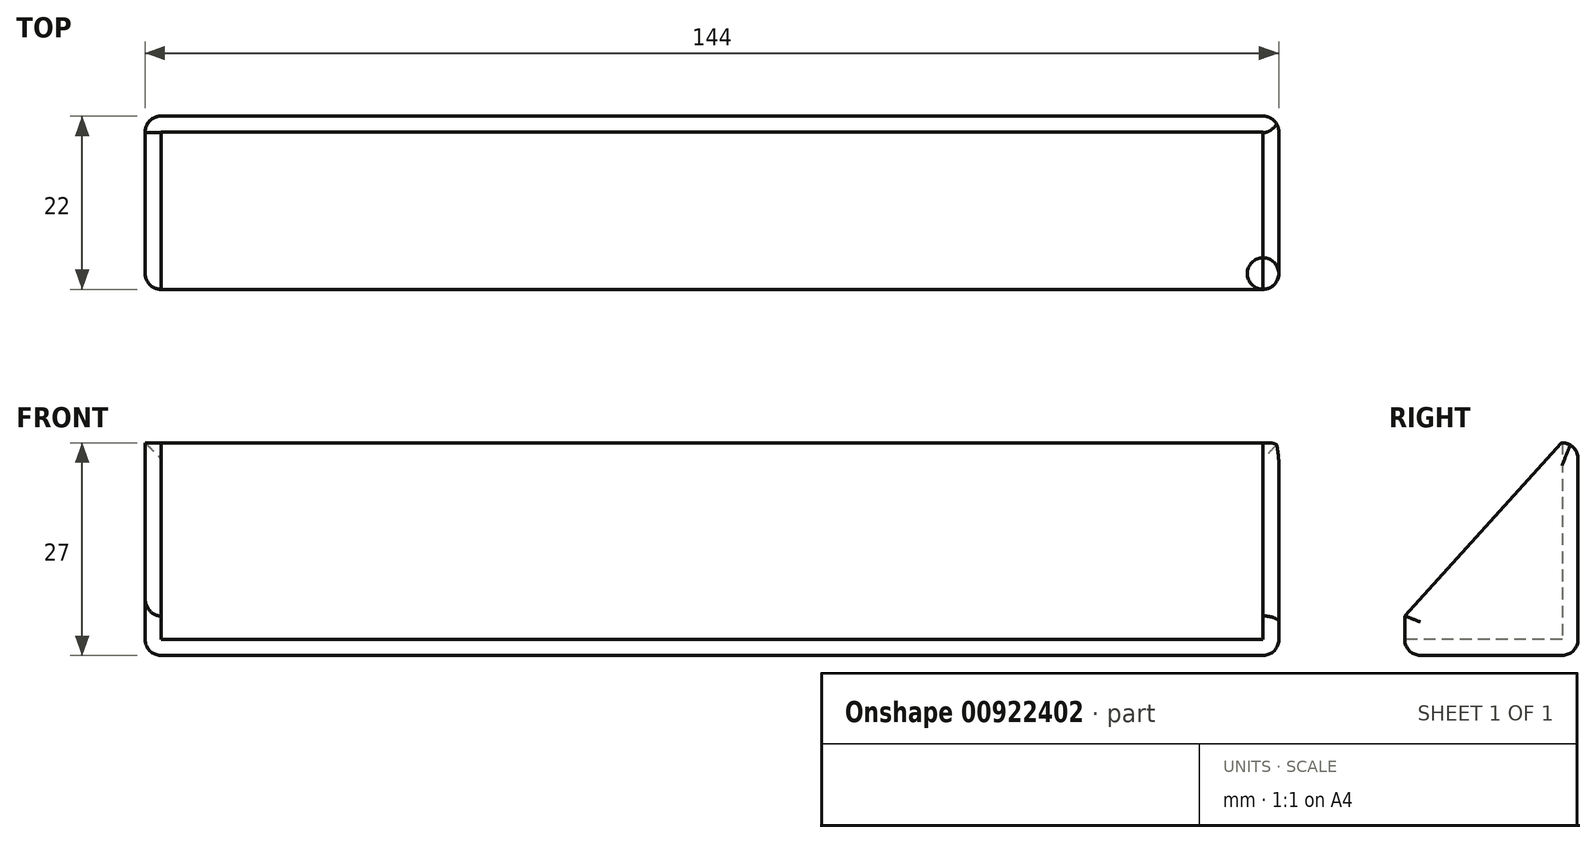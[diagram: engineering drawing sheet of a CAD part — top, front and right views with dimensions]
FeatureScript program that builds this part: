
annotation { "Feature Type Name" : "Feature", "Feature Type Description" : "" }
export const myFeature = defineFeature(function(context is Context, id is Id, definition is map)
    precondition{}
    {
        {
            var Q0;
            Q0=qCreatedBy(makeId("Top.planeOp"),FACE);
            var sketch = newSketch(context, id + "F0", { "sketchPlane" : qUnion([Q0])});
            skLineSegment(sketch, "E0.bottom", {"start": v(72, 11) * mm, "end": v(-72, 11) * mm});
            skLineSegment(sketch, "E0.top", {"start": v(72, -11) * mm, "end": v(-72, -11) * mm});
            skLineSegment(sketch, "E0.left", {"start": v(72, 11) * mm, "end": v(72, -11) * mm});
            skLineSegment(sketch, "E0.right", {"start": v(-72, 11) * mm, "end": v(-72, -11) * mm});
            skPoint(sketch, "E0.middle", {"position": v(0, 0) * mm});
            skSolve(sketch);
        }
        {
            var Q0;
            Q0 = qSketchRegion(id + "F0", true);
            extrude(context, id + "F1", {"entities" : qUnion([Q0]), "depth" : 2 * mm, "offsetDistance" : 25 * mm});
        }
        {
            var Q0;
            Q0=makeQuery(id+"F1.opExtrude","CAP_FACE",FACE,{"disambiguationData":[OSD([sQuery(id+"F0.wireOp",EDGE,"E0.bottom"),sQuery(id+"F0.wireOp",EDGE,"E0.top"),sQuery(id+"F0.wireOp",EDGE,"E0.left"),sQuery(id+"F0.wireOp",EDGE,"E0.right")])],"isStart":false});
            var sketch = newSketch(context, id + "F2", { "sketchPlane" : qUnion([Q0])});
            skLineSegment(sketch, "E1.0", {"start": v(-70, 9) * mm, "end": v(-70, -11) * mm});
            skLineSegment(sketch, "E1.1", {"start": v(70, 9) * mm, "end": v(-70, 9) * mm});
            skLineSegment(sketch, "E1.2", {"start": v(70, 9) * mm, "end": v(70, -11) * mm});
            skLineSegment(sketch, "E2", {"start": v(-72, -11) * mm, "end": v(-70, -11) * mm});
            skLineSegment(sketch, "E3", {"start": v(70, -11) * mm, "end": v(72, -11) * mm});
            skSolve(sketch);
        }
        {
            var Q0;
            Q0 = qSketchRegion(id + "F2", true);
            var Q1;
            Q1=makeQuery(id+"F2.imprint","IMPRINT",FACE,{"disambiguationData":[TD([[makeQuery(id+"F2.imprint","IMPRINT",EDGE,{"derivedFrom":sQuery(id+"F2.wireOp",EDGE,"E1.0")}),-1.0]])]});
            extrude(context, id + "F3", {"entities" : qUnion([Q0, Q1]), "operationType" : NewBodyOperationType.ADD, "depth" : 25 * mm, "offsetDistance" : 25 * mm});
        }
        {
            var Q0;
            {var subQ0=sQuery(id+"F0.wireOp",EDGE,"E0.right");Q0=makeQuery(id+"F3.boolean.opBoolean","MERGE",FACE,{"derivedFrom":[makeQuery(id+"F1.opExtrude","SWEPT_FACE",FACE,{"disambiguationData":[OSD([subQ0])]}),makeQuery(id+"F3.opExtrude","SWEPT_FACE",FACE,{"disambiguationData":[OSD([subQ0])]})]});}
            var sketch = newSketch(context, id + "F4", { "sketchPlane" : qUnion([Q0])});
            skLineSegment(sketch, "E4", {"start": v(-8.9, 27) * mm, "end": v(11, 5) * mm});
            skSolve(sketch);
        }
        {
            var Q0;
            Q0 = qSketchRegion(id + "F4", true);
            var Q1;
            {var subQ0=sQuery(id+"F4.wireOp",EDGE,"E4");Q1=makeQuery(id+"F4.imprint","IMPRINT",FACE,{"disambiguationData":[TD([[makeQuery(id+"F4.imprint","IMPRINT",EDGE,{"derivedFrom":subQ0}),1.0]])]});}
            extrude(context, id + "F5", {"entities" : qUnion([Q0, Q1]), "operationType" : NewBodyOperationType.REMOVE, "oppositeDirection" : true, "depth" : 160 * mm, "offsetDistance" : 25 * mm});
        }
        {
            var Q0;
            Q0=makeQuery(id+"F1.opExtrude","CAP_FACE",FACE,{"disambiguationData":[OSD([sQuery(id+"F0.wireOp",EDGE,"E0.bottom"),sQuery(id+"F0.wireOp",EDGE,"E0.top"),sQuery(id+"F0.wireOp",EDGE,"E0.left"),sQuery(id+"F0.wireOp",EDGE,"E0.right")])],"isStart":true});
            var Q1;
            {var subQ0=sQuery(id+"F0.wireOp",EDGE,"E0.right");var subQ1=sQuery(id+"F0.wireOp",EDGE,"E0.bottom");Q1=makeQuery(id+"F3.boolean.opBoolean","MERGE",EDGE,{"derivedFrom":[makeQuery(id+"F1.opExtrude","SWEPT_EDGE",EDGE,{"disambiguationData":[OSD([subQ1,subQ0])]}),makeQuery(id+"F3.opExtrude","SWEPT_EDGE",EDGE,{"disambiguationData":[OSD([subQ1,subQ0])]})]});}
            var Q2;
            {var subQ0=sQuery(id+"F0.wireOp",EDGE,"E0.left");var subQ1=sQuery(id+"F0.wireOp",EDGE,"E0.bottom");Q2=makeQuery(id+"F3.boolean.opBoolean","MERGE",EDGE,{"derivedFrom":[makeQuery(id+"F1.opExtrude","SWEPT_EDGE",EDGE,{"disambiguationData":[OSD([subQ1,subQ0])]}),makeQuery(id+"F3.opExtrude","SWEPT_EDGE",EDGE,{"disambiguationData":[OSD([subQ1,subQ0])]})]});}
            var Q3;
            {var subQ0=sQuery(id+"F0.wireOp",EDGE,"E0.left");Q3=makeQuery(id+"F5.boolean.opBoolean","INTERSECT",EDGE,{"derivedFrom":[makeQuery(id+"F3.boolean.opBoolean","MERGE",FACE,{"derivedFrom":[makeQuery(id+"F1.opExtrude","SWEPT_FACE",FACE,{"disambiguationData":[OSD([subQ0])]}),makeQuery(id+"F3.opExtrude","SWEPT_FACE",FACE,{"disambiguationData":[OSD([subQ0])]})]}),makeQuery(id+"F5.opExtrude","SWEPT_FACE",FACE,{"disambiguationData":[OSD([sQuery(id+"F4.wireOp",EDGE,"E4")])]})]});}
            var Q4;
            Q4=makeQuery(id+"F5.boolean.opBoolean","COPY",EDGE,{"derivedFrom":makeQuery(id+"F5.opExtrude","CAP_EDGE",EDGE,{"disambiguationData":[OSD([sQuery(id+"F4.wireOp",EDGE,"E4")])],"isStart":true})});
            var Q5;
            {var subQ0=sQuery(id+"F0.wireOp",EDGE,"E0.right");Q5=makeQuery(id+"F3.boolean.opBoolean","MERGE",EDGE,{"derivedFrom":[makeQuery(id+"F1.opExtrude","SWEPT_EDGE",EDGE,{"disambiguationData":[OSD([sQuery(id+"F0.wireOp",EDGE,"E0.top"),subQ0])]}),makeQuery(id+"F3.opExtrude","SWEPT_EDGE",EDGE,{"disambiguationData":[OSD([subQ0,sQuery(id+"F2.wireOp",EDGE,"E2")])]})]});}
            var Q6;
            {var subQ0=sQuery(id+"F0.wireOp",EDGE,"E0.left");Q6=makeQuery(id+"F3.boolean.opBoolean","MERGE",EDGE,{"derivedFrom":[makeQuery(id+"F1.opExtrude","SWEPT_EDGE",EDGE,{"disambiguationData":[OSD([sQuery(id+"F0.wireOp",EDGE,"E0.top"),subQ0])]}),makeQuery(id+"F3.opExtrude","SWEPT_EDGE",EDGE,{"disambiguationData":[OSD([subQ0,sQuery(id+"F2.wireOp",EDGE,"E3")])]})]});}
            var Q7;
            Q7=makeQuery(id+"F3.opExtrude","CAP_EDGE",EDGE,{"disambiguationData":[OSD([sQuery(id+"F0.wireOp",EDGE,"E0.bottom")])],"isStart":false});
            fillet(context, id + "F6", {"entities" : qUnion([Q0, Q1, Q2, Q3, Q4, Q5, Q6, Q7]), "radius" : 2 * mm, "tangentPropagation" : true, "allowEdgeOverflow" : false});
        }
    });
